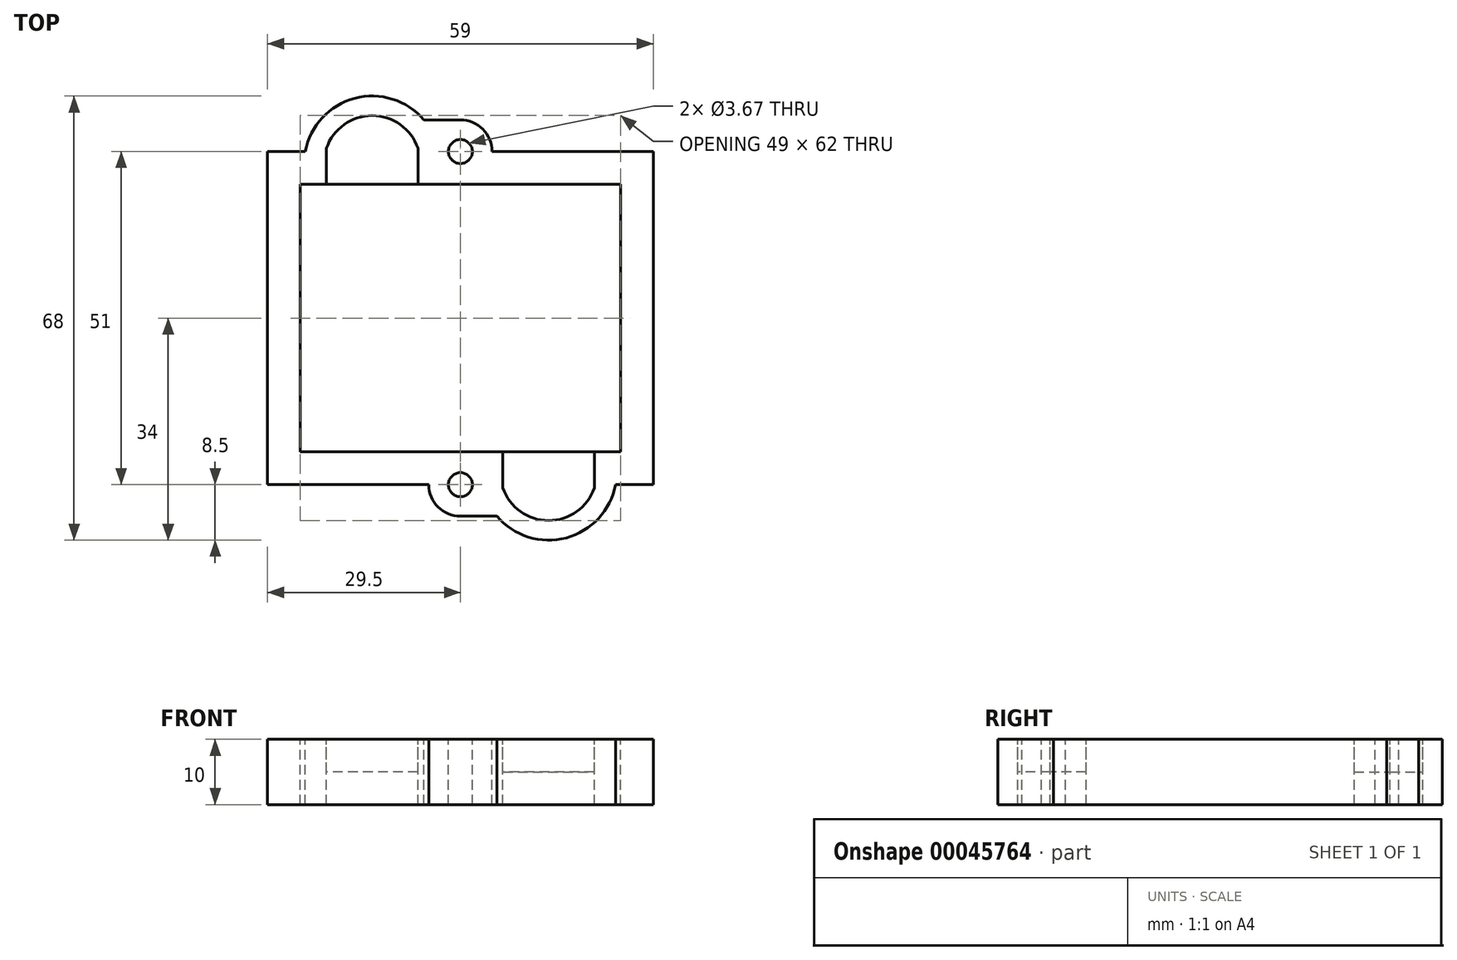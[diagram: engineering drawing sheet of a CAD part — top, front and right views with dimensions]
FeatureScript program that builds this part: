
annotation { "Feature Type Name" : "Feature", "Feature Type Description" : "" }
export const myFeature = defineFeature(function(context is Context, id is Id, definition is map)
    precondition{}
    {
        {
            var Q0;
            Q0=qCreatedBy(makeId("Top.planeOp"),FACE);
            var sketch = newSketch(context, id + "F2", { "sketchPlane" : qUnion([Q0])});
            skLineSegment(sketch, "E0.rect.bottom", {"start": v(24.5, 20.5) * mm, "end": v(-24.5, 20.5) * mm});
            skLineSegment(sketch, "E0.rect.top", {"start": v(24.5, -20.5) * mm, "end": v(-24.5, -20.5) * mm});
            skLineSegment(sketch, "E0.rect.left", {"start": v(24.5, 20.5) * mm, "end": v(24.5, -20.5) * mm});
            skLineSegment(sketch, "E0.rect.right", {"start": v(-24.5, 20.5) * mm, "end": v(-24.5, -20.5) * mm});
            skPoint(sketch, "E0.rect.middle", {"position": v(0, 0) * mm});
            skLineSegment(sketch, "E1.bottom", {"start": v(-24.5, 20.5) * mm, "end": v(-6.5, 20.5) * mm});
            skLineSegment(sketch, "E1.right", {"start": v(-6.5, 20.5) * mm, "end": v(-6.5, 26) * mm});
            skLineSegment(sketch, "E2.bottom", {"start": v(24.5, -20.5) * mm, "end": v(6.5, -20.5) * mm});
            skLineSegment(sketch, "E2.right", {"start": v(6.5, -20.5) * mm, "end": v(6.5, -26) * mm});
            skPoint(sketch, "E3.first.point", {"position": v(-20.5, 26) * mm});
            skPoint(sketch, "E3.second.point", {"position": v(-6.5, 26) * mm});
            skPoint(sketch, "E3.third.point", {"position": v(-13.5, 31) * mm});
            skArc(sketch, "E4.trimOffspring", {"start": v(-6.5, 26) * mm, "mid": v(-13.5, 31) * mm, "end": v(-20.5, 26) * mm});
            skLineSegment(sketch, "E5", {"start": v(-24.5, 0) * mm, "end": v(24.5, 0) * mm, "construction": true});
            skLineSegment(sketch, "E6.MirrorCS", {"start": v(24.5, -20.5) * mm, "end": v(24.5, 20.5) * mm});
            skPoint(sketch, "E7.first.point", {"position": v(20.5, -26) * mm});
            skPoint(sketch, "E7.second.point", {"position": v(6.5, -26) * mm});
            skArc(sketch, "E8.trimOffspring", {"start": v(6.5, -26) * mm, "mid": v(13.5, -31) * mm, "end": v(20.5, -26) * mm});
            skLineSegment(sketch, "E9", {"start": v(0, 0) * mm, "end": v(0, 20.5) * mm, "construction": true});
            skLineSegment(sketch, "E10", {"start": v(0, 0) * mm, "end": v(0, -20.5) * mm, "construction": true});
            skLineSegment(sketch, "E11", {"start": v(6.75, 25.5) * mm, "end": v(6.75, 25.5) * mm});
            skLineSegment(sketch, "E12.rect.bottom", {"start": v(29.5, 25.5) * mm, "end": v(6.75, 25.5) * mm});
            skLineSegment(sketch, "E12.rect.top", {"start": v(29.5, -25.5) * mm, "end": v(23.72, -25.5) * mm});
            skLineSegment(sketch, "E12.rect.left", {"start": v(29.5, 25.5) * mm, "end": v(29.5, -25.5) * mm});
            skLineSegment(sketch, "E12.rect.right", {"start": v(-29.5, 25.5) * mm, "end": v(-29.5, -25.5) * mm});
            skArc(sketch, "E13", {"start": v(-5.58, 30.34) * mm, "mid": v(-16.18, 33.65) * mm, "end": v(-23.72, 25.5) * mm});
            skLineSegment(sketch, "E14.trimOffspring", {"start": v(-23.72, 25.5) * mm, "end": v(-29.5, 25.5) * mm});
            skArc(sketch, "E15", {"start": v(5.58, -30.34) * mm, "mid": v(16.18, -33.65) * mm, "end": v(23.72, -25.5) * mm});
            skLineSegment(sketch, "E16.trimOffspring", {"start": v(-10.75, -25.5) * mm, "end": v(-29.5, -25.5) * mm});
            skPoint(sketch, "E17.orphan", {"position": v(13.5, -31) * mm});
            skCircle(sketch, "E18", {"center": v(0, -25.5) * mm, "radius": 1.84 * mm});
            skLineSegment(sketch, "E19", {"start": v(0, 20.5) * mm, "end": v(0, 37.63) * mm, "construction": true});
            skCircle(sketch, "E20", {"center": v(0, 25.5) * mm, "radius": 1.84 * mm});
            skLineSegment(sketch, "E21", {"start": v(20.5, -20.5) * mm, "end": v(20.5, -26) * mm});
            skLineSegment(sketch, "E22", {"start": v(-20.5, 20.5) * mm, "end": v(-20.5, 26) * mm});
            skLineSegment(sketch, "E23", {"start": v(0, -30.34) * mm, "end": v(5.58, -30.34) * mm});
            skArc(sketch, "E24", {"start": v(-4.84, -25.5) * mm, "mid": v(-3.42, -28.92) * mm, "end": v(0, -30.34) * mm});
            skLineSegment(sketch, "E25", {"start": v(-10.75, -25.5) * mm, "end": v(-4.84, -25.5) * mm});
            skArc(sketch, "E26", {"start": v(4.84, 25.5) * mm, "mid": v(3.42, 28.92) * mm, "end": v(0, 30.34) * mm});
            skLineSegment(sketch, "E27", {"start": v(-5.58, 30.34) * mm, "end": v(0, 30.34) * mm});
            skLineSegment(sketch, "E28", {"start": v(6.75, 25.5) * mm, "end": v(4.84, 25.5) * mm});
            skSolve(sketch);
        }
        {
            var Q0;
            Q0=makeQuery(id+"F2.imprint","IMPRINT",FACE,{"disambiguationData":[TD([[makeQuery(id+"F2.imprint","IMPRINT",EDGE,{"derivedFrom":sQuery(id+"F2.wireOp",EDGE,"E0.rect.bottom")}),-1.0]])]});
            extrude(context, id + "F0", {"entities" : qUnion([Q0]), "oppositeDirection" : true, "depth" : 10 * mm});
        }
        {
            var Q0;
            {var subQ0=sQuery(id+"F2.wireOp",EDGE,"E1.right");Q0=makeQuery(id+"F2.imprint","IMPRINT",FACE,{"disambiguationData":[TD([[makeQuery(id+"F2.imprint","IMPRINT",EDGE,{"derivedFrom":subQ0}),1.0]])]});}
            var Q1;
            {var subQ2=sQuery(id+"F2.wireOp",EDGE,"E2.right");Q1=makeQuery(id+"F2.imprint","IMPRINT",FACE,{"disambiguationData":[TD([[makeQuery(id+"F2.imprint","IMPRINT",EDGE,{"derivedFrom":subQ2}),1.0]])]});}
            extrude(context, id + "F1", {"entities" : qUnion([Q0, Q1]), "oppositeDirection" : true, "depth" : 5 * mm});
        }
    });
